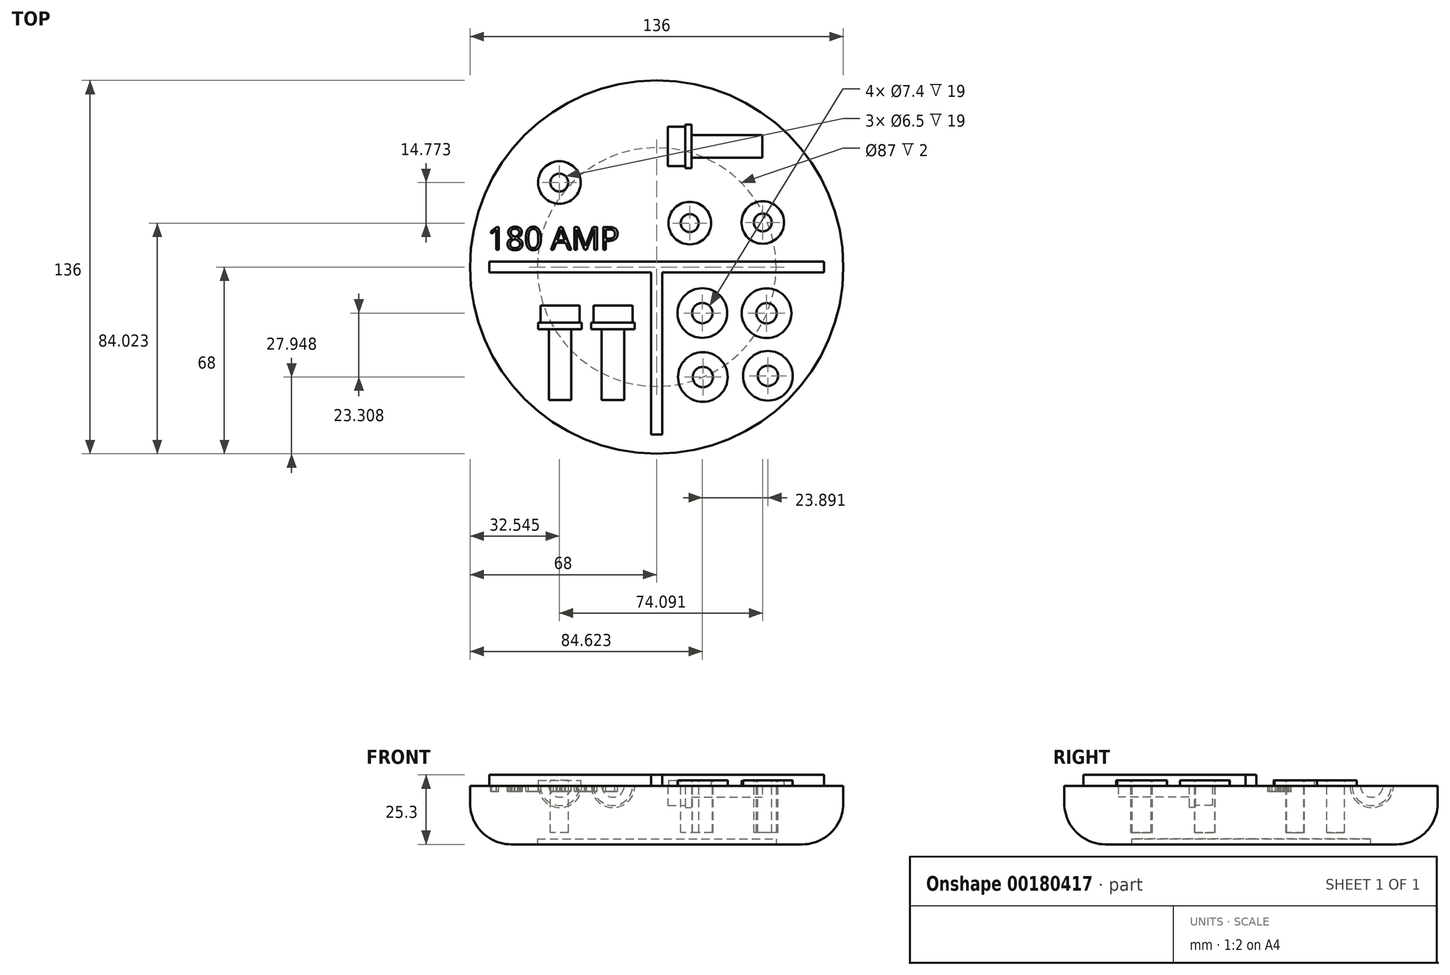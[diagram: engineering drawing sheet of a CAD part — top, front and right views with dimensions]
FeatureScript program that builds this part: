
annotation { "Feature Type Name" : "Feature", "Feature Type Description" : "" }
export const myFeature = defineFeature(function(context is Context, id is Id, definition is map)
    precondition{}
    {
        {
            var Q0;
            Q0=qCreatedBy(makeId("Front.planeOp"),FACE);
            var sketch = newSketch(context, id + "F0", { "sketchPlane" : qUnion([Q0])});
            skLineSegment(sketch, "E0.bottom", {"start": v(0, 0) * mm, "end": v(-68, 0) * mm});
            skLineSegment(sketch, "E0.top", {"start": v(0, -21.3) * mm, "end": v(-53, -21.3) * mm});
            skLineSegment(sketch, "E0.left", {"start": v(0, 0) * mm, "end": v(0, -21.3) * mm});
            skLineSegment(sketch, "E0.right", {"start": v(-68, 0) * mm, "end": v(-68, -6.3) * mm});
            skLineSegment(sketch, "E1.bottom", {"start": v(0, -21.3) * mm, "end": v(-43, -21.3) * mm});
            skLineSegment(sketch, "E1.top", {"start": v(0, -19.3) * mm, "end": v(-43, -19.3) * mm});
            skLineSegment(sketch, "E1.left", {"start": v(0, -21.3) * mm, "end": v(0, -19.3) * mm});
            skLineSegment(sketch, "E1.right", {"start": v(-43, -21.3) * mm, "end": v(-43, -19.3) * mm});
            skPoint(sketch, "E2.visualSharp", {"position": v(-68, -21.3) * mm});
            skArc(sketch, "E2.filletArc", {"start": v(-68, -6.3) * mm, "mid": v(-63.6, -16.9) * mm, "end": v(-53, -21.3) * mm});
            skSolve(sketch);
        }
        {
            var Q0;
            Q0=qSketchRegion(id+"F0",true);
            var Q1;
            Q1=sQuery(id+"F0.wireOp",EDGE,"E1.left");
            revolve(context, id + "F1", {"entities" : qUnion([Q0]), "axis" : qUnion([Q1]), "revolveType" : RevolveType.FULL});
        }
        {
            var Q0;
            Q0=makeQuery(id+"F1.opRevolve","SWEPT_FACE",FACE,{"disambiguationData":[OSD([sQuery(id+"F0.wireOp",EDGE,"E0.top"),sQuery(id+"F0.wireOp",EDGE,"E1.bottom")])]});
            var sketch = newSketch(context, id + "F2", { "sketchPlane" : qUnion([Q0])});
            skCircle(sketch, "E3", {"center": v(0, 0) * mm, "radius": 43.5 * mm});
            skSolve(sketch);
        }
        {
            var Q0;
            Q0=makeQuery(id+"F2.imprint","IMPRINT",FACE,{"disambiguationData":[TD([[makeQuery(id+"F2.imprint","IMPRINT",EDGE,{"derivedFrom":sQuery(id+"F2.wireOp",EDGE,"E3")}),1.0]])]});
            extrude(context, id + "F3", {"entities" : qUnion([Q0]), "operationType" : NewBodyOperationType.REMOVE, "oppositeDirection" : true, "depth" : 2 * mm});
        }
        {
            var Q0;
            Q0=makeQuery(id+"F1.opRevolve","SWEPT_FACE",FACE,{"disambiguationData":[OSD([sQuery(id+"F0.wireOp",EDGE,"E0.bottom")])]});
            var sketch = newSketch(context, id + "F4", { "sketchPlane" : qUnion([Q0])});
            skLineSegment(sketch, "E4", {"start": v(0, 0) * mm, "end": v(0, -68) * mm, "construction": true});
            skLineSegment(sketch, "E5.bottom", {"start": v(-2, 1.01) * mm, "end": v(2, 1.01) * mm});
            skLineSegment(sketch, "E5.top", {"start": v(-2, -60.99) * mm, "end": v(2, -60.99) * mm});
            skLineSegment(sketch, "E5.left", {"start": v(-2, 1.01) * mm, "end": v(-2, -60.99) * mm});
            skLineSegment(sketch, "E5.right", {"start": v(2, 1.01) * mm, "end": v(2, -60.99) * mm});
            skLineSegment(sketch, "E6.bottom", {"start": v(-61.02, 2) * mm, "end": v(60.99, 2) * mm});
            skLineSegment(sketch, "E6.top", {"start": v(-61.02, -2) * mm, "end": v(60.99, -2) * mm});
            skLineSegment(sketch, "E6.left", {"start": v(-61.02, 2) * mm, "end": v(-61.02, -2) * mm});
            skLineSegment(sketch, "E6.right", {"start": v(60.99, 2) * mm, "end": v(60.99, -2) * mm});
            skSolve(sketch);
        }
        {
            var Q0;
            {var subQ1=sQuery(id+"F4.wireOp",EDGE,"E5.bottom");Q0=makeQuery(id+"F4.imprint","IMPRINT",FACE,{"disambiguationData":[TD([[makeQuery(id+"F4.imprint","IMPRINT",EDGE,{"derivedFrom":subQ1}),1.0]])]});}
            var Q1;
            Q1=qSketchRegion(id+"F4",true);
            extrude(context, id + "F5", {"entities" : qUnion([Q0, Q1]), "operationType" : NewBodyOperationType.ADD, "depth" : 4 * mm});
        }
        {
            var Q0;
            Q0=makeQuery(id+"F1.opRevolve","SWEPT_FACE",FACE,{"disambiguationData":[OSD([sQuery(id+"F0.wireOp",EDGE,"E0.bottom")])]});
            var sketch = newSketch(context, id + "F6", { "sketchPlane" : qUnion([Q0])});
            skText(sketch, "E7", { "text": "180 AMP", "fontName": "OpenSans-Regular.ttf"});
            const initialGuessF6  = {"E7": [-0.0616, 0.00625, 1, 0, 0.0084]};
            skSetInitialGuess(sketch, initialGuessF6);
            skSolve(sketch);
        }
        {
            var Q0;
            Q0=qSketchRegion(id+"F6",true);
            extrude(context, id + "F7", {"entities" : qUnion([Q0]), "operationType" : NewBodyOperationType.REMOVE, "oppositeDirection" : true, "depth" : 2 * mm});
        }
        {
            var Q0;
            Q0=makeQuery(id+"F7.boolean.opBoolean","SPLIT",FACE,{"disambiguationData":[TD([makeQuery(id+"F1.opRevolve","SWEPT_FACE",FACE,{"disambiguationData":[OSD([sQuery(id+"F0.wireOp",EDGE,"E0.right")])]})])],"derivedFrom":makeQuery(id+"F1.opRevolve","SWEPT_FACE",FACE,{"disambiguationData":[OSD([sQuery(id+"F0.wireOp",EDGE,"E0.bottom")])]})});
            var sketch = newSketch(context, id + "F8", { "sketchPlane" : qUnion([Q0])});
            skCircle(sketch, "E8", {"center": v(-35.45, 30.8) * mm, "radius": 7.75 * mm});
            skSolve(sketch);
        }
        {
            var Q0;
            Q0=makeQuery(id+"F8.imprint","IMPRINT",FACE,{"disambiguationData":[TD([[makeQuery(id+"F8.imprint","IMPRINT",EDGE,{"derivedFrom":sQuery(id+"F8.wireOp",EDGE,"E8")}),1.0]])]});
            var sketch = newSketch(context, id + "F9", { "sketchPlane" : qUnion([Q0])});
            skSolve(sketch);
        }
        {
            var Q0;
            Q0=makeQuery(id+"F9.imprint","IMPRINT",FACE,{"disambiguationData":[TD([[makeQuery(id+"F9.imprint","IMPRINT",EDGE,{"derivedFrom":makeQuery(id+"F8.imprint","IMPRINT",EDGE,{"derivedFrom":sQuery(id+"F8.wireOp",EDGE,"E8")})}),1.0]])]});
            var Q1;
            Q1=qConstructionFilter(qBodyType(qCreatedBy(id+"F9",EDGE),BodyType.WIRE),ConstructionObject.NO);
            extrude(context, id + "F10", {"entities" : qUnion([Q0]), "operationType" : NewBodyOperationType.ADD, "surfaceEntities" : qUnion([Q1]), "depth" : 2 * mm});
        }
        {
            var Q0;
            Q0=makeQuery(id+"F8.imprint","IMPRINT",FACE,{"disambiguationData":[TD([[makeQuery(id+"F8.imprint","IMPRINT",EDGE,{"derivedFrom":sQuery(id+"F8.wireOp",EDGE,"E8")}),1.0]])]});
            extrude(context, id + "F11", {"entities" : qUnion([Q0]), "operationType" : NewBodyOperationType.ADD, "depth" : 2 * mm});
        }
        {
            var Q0;
            Q0=makeQuery(id+"F10.opExtrude","CAP_FACE",FACE,{"disambiguationData":[OSD([sQuery(id+"F8.wireOp",EDGE,"E8")])],"isStart":false});
            var sketch = newSketch(context, id + "F12", { "sketchPlane" : qUnion([Q0])});
            skCircle(sketch, "E9", {"center": v(-35.45, 30.8) * mm, "radius": 3.25 * mm});
            skSolve(sketch);
        }
        {
            var Q0;
            Q0=makeQuery(id+"F12.imprint","IMPRINT",FACE,{"disambiguationData":[TD([[makeQuery(id+"F12.imprint","IMPRINT",EDGE,{"derivedFrom":sQuery(id+"F12.wireOp",EDGE,"E9")}),1.0]])]});
            extrude(context, id + "F13", {"entities" : qUnion([Q0]), "operationType" : NewBodyOperationType.REMOVE, "oppositeDirection" : true, "depth" : 19 * mm});
        }
        {
            var Q0;
            Q0=makeQuery(id+"F7.boolean.opBoolean","SPLIT",FACE,{"disambiguationData":[TD([makeQuery(id+"F1.opRevolve","SWEPT_FACE",FACE,{"disambiguationData":[OSD([sQuery(id+"F0.wireOp",EDGE,"E0.right")])]})])],"derivedFrom":makeQuery(id+"F1.opRevolve","SWEPT_FACE",FACE,{"disambiguationData":[OSD([sQuery(id+"F0.wireOp",EDGE,"E0.bottom")])]})});
            var sketch = newSketch(context, id + "F14", { "sketchPlane" : qUnion([Q0])});
            skCircle(sketch, "E10", {"center": v(12.05, 16.02) * mm, "radius": 7.75 * mm});
            skSolve(sketch);
        }
        {
            var Q0;
            Q0=qSketchRegion(id+"F14",true);
            extrude(context, id + "F15", {"entities" : qUnion([Q0]), "operationType" : NewBodyOperationType.ADD, "depth" : 2 * mm});
        }
        {
            var Q0;
            Q0=makeQuery(id+"F15.opExtrude","CAP_FACE",FACE,{"disambiguationData":[OSD([sQuery(id+"F14.wireOp",EDGE,"E10")])],"isStart":false});
            var sketch = newSketch(context, id + "F16", { "sketchPlane" : qUnion([Q0])});
            skCircle(sketch, "E11", {"center": v(12.05, 16.02) * mm, "radius": 3.25 * mm});
            skSolve(sketch);
        }
        {
            var Q0;
            Q0=qSketchRegion(id+"F16",true);
            extrude(context, id + "F17", {"entities" : qUnion([Q0]), "operationType" : NewBodyOperationType.REMOVE, "oppositeDirection" : true, "depth" : 19 * mm});
        }
        {
            var Q0;
            Q0=makeQuery(id+"F7.boolean.opBoolean","SPLIT",FACE,{"disambiguationData":[TD([makeQuery(id+"F1.opRevolve","SWEPT_FACE",FACE,{"disambiguationData":[OSD([sQuery(id+"F0.wireOp",EDGE,"E0.right")])]})])],"derivedFrom":makeQuery(id+"F1.opRevolve","SWEPT_FACE",FACE,{"disambiguationData":[OSD([sQuery(id+"F0.wireOp",EDGE,"E0.bottom")])]})});
            var sketch = newSketch(context, id + "F18", { "sketchPlane" : qUnion([Q0])});
            skCircle(sketch, "E12", {"center": v(38.64, 16.25) * mm, "radius": 7.75 * mm});
            skSolve(sketch);
        }
        {
            var Q0;
            Q0=qSketchRegion(id+"F18",true);
            extrude(context, id + "F19", {"entities" : qUnion([Q0]), "operationType" : NewBodyOperationType.ADD, "depth" : 2 * mm});
        }
        {
            var Q0;
            Q0=makeQuery(id+"F19.opExtrude","CAP_FACE",FACE,{"disambiguationData":[OSD([sQuery(id+"F18.wireOp",EDGE,"E12")])],"isStart":false});
            var sketch = newSketch(context, id + "F20", { "sketchPlane" : qUnion([Q0])});
            skCircle(sketch, "E13", {"center": v(38.64, 16.25) * mm, "radius": 3.25 * mm});
            skSolve(sketch);
        }
        {
            var Q0;
            Q0=qSketchRegion(id+"F20",true);
            extrude(context, id + "F21", {"entities" : qUnion([Q0]), "operationType" : NewBodyOperationType.REMOVE, "oppositeDirection" : true, "depth" : 19 * mm});
        }
        {
            var Q0;
            Q0=makeQuery(id+"F7.boolean.opBoolean","SPLIT",FACE,{"disambiguationData":[TD([makeQuery(id+"F1.opRevolve","SWEPT_FACE",FACE,{"disambiguationData":[OSD([sQuery(id+"F0.wireOp",EDGE,"E0.right")])]})])],"derivedFrom":makeQuery(id+"F1.opRevolve","SWEPT_FACE",FACE,{"disambiguationData":[OSD([sQuery(id+"F0.wireOp",EDGE,"E0.bottom")])]})});
            var sketch = newSketch(context, id + "F22", { "sketchPlane" : qUnion([Q0])});
            skLineSegment(sketch, "E14", {"start": v(4.1, 43.98) * mm, "end": v(38.44, 43.98) * mm, "construction": true});
            skLineSegment(sketch, "E15.bottom", {"start": v(4.1, 43.98) * mm, "end": v(10.34, 43.98) * mm});
            skLineSegment(sketch, "E15.top", {"start": v(4.1, 36.85) * mm, "end": v(10.34, 36.85) * mm});
            skLineSegment(sketch, "E15.left", {"start": v(4.1, 43.98) * mm, "end": v(4.1, 36.85) * mm});
            skLineSegment(sketch, "E15.right", {"start": v(10.34, 40.41) * mm, "end": v(10.34, 36.85) * mm});
            skPoint(sketch, "E16.oppositeSnap0", {"position": v(10.34, 40.41) * mm});
            skLineSegment(sketch, "E16.bottom", {"start": v(10.34, 43.98) * mm, "end": v(12.7, 43.98) * mm});
            skLineSegment(sketch, "E16.top", {"start": v(10.34, 36.05) * mm, "end": v(12.7, 36.05) * mm});
            skLineSegment(sketch, "E16.left", {"start": v(10.34, 36.85) * mm, "end": v(10.34, 36.05) * mm});
            skLineSegment(sketch, "E16.right", {"start": v(12.7, 39.88) * mm, "end": v(12.7, 36.05) * mm});
            skLineSegment(sketch, "E17.bottom", {"start": v(12.7, 43.98) * mm, "end": v(38.44, 43.98) * mm});
            skLineSegment(sketch, "E17.top", {"start": v(12.7, 39.88) * mm, "end": v(38.44, 39.88) * mm});
            skLineSegment(sketch, "E17.right", {"start": v(38.44, 43.98) * mm, "end": v(38.44, 39.88) * mm});
            skPoint(sketch, "E18.orphan", {"position": v(0, 43.98) * mm});
            skSolve(sketch);
        }
        {
            var Q0;
            Q0=makeQuery(id+"F22.imprint","IMPRINT",FACE,{"disambiguationData":[TD([[makeQuery(id+"F22.imprint","IMPRINT",EDGE,{"derivedFrom":sQuery(id+"F22.wireOp",EDGE,"E15.bottom")}),-1.0]])]});
            var Q1;
            Q1=sQuery(id+"F22.wireOp",EDGE,"E17.bottom");
            revolve(context, id + "F23", {"operationType" : NewBodyOperationType.REMOVE, "entities" : qUnion([Q0]), "axis" : qUnion([Q1]), "revolveType" : RevolveType.FULL, "oppositeDirection" : true});
        }
        {
            var Q0;
            Q0=makeQuery(id+"F7.boolean.opBoolean","SPLIT",FACE,{"disambiguationData":[TD([makeQuery(id+"F1.opRevolve","SWEPT_FACE",FACE,{"disambiguationData":[OSD([sQuery(id+"F0.wireOp",EDGE,"E0.right")])]})])],"derivedFrom":makeQuery(id+"F1.opRevolve","SWEPT_FACE",FACE,{"disambiguationData":[OSD([sQuery(id+"F0.wireOp",EDGE,"E0.bottom")])]})});
            var sketch = newSketch(context, id + "F24", { "sketchPlane" : qUnion([Q0])});
            skLineSegment(sketch, "E19", {"start": v(-8.8, -14.01) * mm, "end": v(-15.93, -14.01) * mm, "construction": true});
            skLineSegment(sketch, "E20.left", {"start": v(-8.8, -14.01) * mm, "end": v(-8.8, -20.26) * mm, "construction": true});
            skLineSegment(sketch, "E20.right", {"start": v(-15.93, -14.01) * mm, "end": v(-15.93, -20.26) * mm, "construction": true});
            skLineSegment(sketch, "E21.bottom", {"start": v(-8.8, -20.26) * mm, "end": v(-8, -20.26) * mm, "construction": true});
            skLineSegment(sketch, "E21.top", {"start": v(-11.83, -22.61) * mm, "end": v(-8, -22.61) * mm, "construction": true});
            skLineSegment(sketch, "E21.left", {"start": v(-15.93, -20.26) * mm, "end": v(-15.93, -22.61) * mm, "construction": true});
            skLineSegment(sketch, "E21.right", {"start": v(-8, -20.26) * mm, "end": v(-8, -22.61) * mm, "construction": true});
            skLineSegment(sketch, "E22.top", {"start": v(-15.93, -48.36) * mm, "end": v(-11.83, -48.36) * mm});
            skLineSegment(sketch, "E22.left", {"start": v(-15.93, -22.61) * mm, "end": v(-15.93, -48.36) * mm});
            skLineSegment(sketch, "E22.right", {"start": v(-11.83, -22.61) * mm, "end": v(-11.83, -48.36) * mm});
            skLineSegment(sketch, "E23.bottom", {"start": v(-15.93, -14.01) * mm, "end": v(-8.8, -14.01) * mm});
            skLineSegment(sketch, "E23.left", {"start": v(-15.93, -14.01) * mm, "end": v(-15.93, -20.26) * mm});
            skLineSegment(sketch, "E23.right", {"start": v(-8.8, -14.01) * mm, "end": v(-8.8, -20.26) * mm});
            skLineSegment(sketch, "E24.bottom", {"start": v(-8, -20.26) * mm, "end": v(-8.8, -20.26) * mm});
            skLineSegment(sketch, "E24.top", {"start": v(-8, -22.61) * mm, "end": v(-11.83, -22.61) * mm});
            skLineSegment(sketch, "E24.left", {"start": v(-8, -20.26) * mm, "end": v(-8, -22.61) * mm});
            skLineSegment(sketch, "E24.right", {"start": v(-15.93, -20.26) * mm, "end": v(-15.93, -22.61) * mm});
            skSolve(sketch);
        }
        {
            var Q0;
            Q0=qSketchRegion(id+"F24",true);
            var Q1;
            Q1=sQuery(id+"F24.wireOp",EDGE,"E22.left");
            revolve(context, id + "F25", {"operationType" : NewBodyOperationType.REMOVE, "entities" : qUnion([Q0]), "axis" : qUnion([Q1]), "revolveType" : RevolveType.FULL, "oppositeDirection" : true});
        }
        {
            var Q0;
            Q0=makeQuery(id+"F7.boolean.opBoolean","SPLIT",FACE,{"disambiguationData":[TD([makeQuery(id+"F1.opRevolve","SWEPT_FACE",FACE,{"disambiguationData":[OSD([sQuery(id+"F0.wireOp",EDGE,"E0.right")])]})])],"derivedFrom":makeQuery(id+"F1.opRevolve","SWEPT_FACE",FACE,{"disambiguationData":[OSD([sQuery(id+"F0.wireOp",EDGE,"E0.bottom")])]})});
            var sketch = newSketch(context, id + "F26", { "sketchPlane" : qUnion([Q0])});
            skLineSegment(sketch, "E25", {"start": v(-8.8, -14.01) * mm, "end": v(-54.14, -14.01) * mm, "construction": true});
            skLineSegment(sketch, "E26.bottom", {"start": v(-28.05, -14.01) * mm, "end": v(-35.2, -14.01) * mm, "construction": true});
            skLineSegment(sketch, "E26.left", {"start": v(-28.05, -14.01) * mm, "end": v(-28.05, -20.26) * mm, "construction": true});
            skLineSegment(sketch, "E26.right", {"start": v(-35.2, -14.01) * mm, "end": v(-35.2, -20.26) * mm, "construction": true});
            skLineSegment(sketch, "E27.bottom", {"start": v(-35.2, -14.01) * mm, "end": v(-28.05, -14.01) * mm});
            skLineSegment(sketch, "E27.left", {"start": v(-35.2, -14.01) * mm, "end": v(-35.2, -20.26) * mm});
            skLineSegment(sketch, "E27.right", {"start": v(-28.05, -14.01) * mm, "end": v(-28.05, -20.26) * mm});
            skLineSegment(sketch, "E28.bottom", {"start": v(-28.05, -20.26) * mm, "end": v(-27.28, -20.26) * mm});
            skLineSegment(sketch, "E28.top", {"start": v(-31.1, -22.61) * mm, "end": v(-27.28, -22.61) * mm});
            skLineSegment(sketch, "E28.left", {"start": v(-35.2, -20.26) * mm, "end": v(-35.2, -22.61) * mm});
            skLineSegment(sketch, "E28.right", {"start": v(-27.28, -20.26) * mm, "end": v(-27.28, -22.61) * mm});
            skLineSegment(sketch, "E29.top", {"start": v(-35.2, -48.36) * mm, "end": v(-31.1, -48.36) * mm});
            skLineSegment(sketch, "E29.left", {"start": v(-35.2, -22.61) * mm, "end": v(-35.2, -48.36) * mm});
            skLineSegment(sketch, "E29.right", {"start": v(-31.1, -22.61) * mm, "end": v(-31.1, -48.36) * mm});
            skSolve(sketch);
        }
        {
            var Q0;
            Q0=qSketchRegion(id+"F26",true);
            var Q1;
            Q1=sQuery(id+"F26.wireOp",EDGE,"E29.left");
            revolve(context, id + "F27", {"operationType" : NewBodyOperationType.REMOVE, "entities" : qUnion([Q0]), "axis" : qUnion([Q1]), "revolveType" : RevolveType.FULL, "oppositeDirection" : true});
        }
        {
            var Q0;
            Q0=makeQuery(id+"F7.boolean.opBoolean","SPLIT",FACE,{"disambiguationData":[TD([makeQuery(id+"F1.opRevolve","SWEPT_FACE",FACE,{"disambiguationData":[OSD([sQuery(id+"F0.wireOp",EDGE,"E0.right")])]})])],"derivedFrom":makeQuery(id+"F1.opRevolve","SWEPT_FACE",FACE,{"disambiguationData":[OSD([sQuery(id+"F0.wireOp",EDGE,"E0.bottom")])]})});
            var sketch = newSketch(context, id + "F28", { "sketchPlane" : qUnion([Q0])});
            skCircle(sketch, "E30", {"center": v(16.62, -16.74) * mm, "radius": 9.05 * mm});
            skSolve(sketch);
        }
        {
            var Q0;
            Q0=makeQuery(id+"F28.imprint","IMPRINT",FACE,{"disambiguationData":[TD([[makeQuery(id+"F28.imprint","IMPRINT",EDGE,{"derivedFrom":sQuery(id+"F28.wireOp",EDGE,"E30")}),-1.0]])]});
            var sketch = newSketch(context, id + "F29", { "sketchPlane" : qUnion([Q0])});
            skCircle(sketch, "E31", {"center": v(40.02, -16.81) * mm, "radius": 9.05 * mm});
            skSolve(sketch);
        }
        {
            var Q0;
            Q0=makeQuery(id+"F28.imprint","IMPRINT",FACE,{"disambiguationData":[TD([[makeQuery(id+"F28.imprint","IMPRINT",EDGE,{"derivedFrom":sQuery(id+"F28.wireOp",EDGE,"E30")}),-1.0]])]});
            var sketch = newSketch(context, id + "F30", { "sketchPlane" : qUnion([Q0])});
            skCircle(sketch, "E32", {"center": v(16.82, -40.05) * mm, "radius": 9.05 * mm});
            skSolve(sketch);
        }
        {
            var Q0;
            Q0=makeQuery(id+"F28.imprint","IMPRINT",FACE,{"disambiguationData":[TD([[makeQuery(id+"F28.imprint","IMPRINT",EDGE,{"derivedFrom":sQuery(id+"F28.wireOp",EDGE,"E30")}),-1.0]])]});
            var sketch = newSketch(context, id + "F31", { "sketchPlane" : qUnion([Q0])});
            skCircle(sketch, "E33", {"center": v(40.51, -39.6) * mm, "radius": 9.05 * mm});
            skSolve(sketch);
        }
        {
            var Q0;
            Q0=makeQuery(id+"F28.imprint","IMPRINT",FACE,{"disambiguationData":[TD([[makeQuery(id+"F28.imprint","IMPRINT",EDGE,{"derivedFrom":sQuery(id+"F28.wireOp",EDGE,"E30")}),1.0]])]});
            extrude(context, id + "F32", {"entities" : qUnion([Q0]), "operationType" : NewBodyOperationType.ADD, "depth" : 2 * mm});
        }
        {
            var Q0;
            Q0=makeQuery(id+"F29.imprint","IMPRINT",FACE,{"disambiguationData":[TD([[makeQuery(id+"F29.imprint","IMPRINT",EDGE,{"derivedFrom":sQuery(id+"F29.wireOp",EDGE,"E31")}),1.0]])]});
            var Q1;
            Q1=makeQuery(id+"F30.imprint","IMPRINT",FACE,{"disambiguationData":[TD([[makeQuery(id+"F30.imprint","IMPRINT",EDGE,{"derivedFrom":sQuery(id+"F30.wireOp",EDGE,"E32")}),1.0]])]});
            extrude(context, id + "F33", {"entities" : qUnion([Q0, Q1]), "operationType" : NewBodyOperationType.ADD, "depth" : 2 * mm});
        }
        {
            var Q0;
            Q0=makeQuery(id+"F31.imprint","IMPRINT",FACE,{"disambiguationData":[TD([[makeQuery(id+"F31.imprint","IMPRINT",EDGE,{"derivedFrom":sQuery(id+"F31.wireOp",EDGE,"E33")}),1.0]])]});
            extrude(context, id + "F34", {"entities" : qUnion([Q0]), "operationType" : NewBodyOperationType.ADD, "depth" : 2 * mm});
        }
        {
            var Q0;
            Q0=makeQuery(id+"F32.opExtrude","CAP_FACE",FACE,{"disambiguationData":[OSD([sQuery(id+"F28.wireOp",EDGE,"E30")])],"isStart":false});
            var sketch = newSketch(context, id + "F35", { "sketchPlane" : qUnion([Q0])});
            skCircle(sketch, "E34", {"center": v(16.62, -16.74) * mm, "radius": 3.7 * mm});
            skSolve(sketch);
        }
        {
            var Q0;
            Q0=makeQuery(id+"F33.opExtrude","CAP_FACE",FACE,{"disambiguationData":[OSD([sQuery(id+"F30.wireOp",EDGE,"E32")])],"isStart":false});
            var sketch = newSketch(context, id + "F36", { "sketchPlane" : qUnion([Q0])});
            skCircle(sketch, "E35", {"center": v(16.82, -40.05) * mm, "radius": 3.7 * mm});
            skSolve(sketch);
        }
        {
            var Q0;
            Q0=makeQuery(id+"F34.opExtrude","CAP_FACE",FACE,{"disambiguationData":[OSD([sQuery(id+"F31.wireOp",EDGE,"E33")])],"isStart":false});
            var sketch = newSketch(context, id + "F37", { "sketchPlane" : qUnion([Q0])});
            skCircle(sketch, "E36", {"center": v(40.51, -39.6) * mm, "radius": 3.7 * mm});
            skSolve(sketch);
        }
        {
            var Q0;
            Q0=makeQuery(id+"F33.opExtrude","CAP_FACE",FACE,{"disambiguationData":[OSD([sQuery(id+"F29.wireOp",EDGE,"E31")])],"isStart":false});
            var sketch = newSketch(context, id + "F38", { "sketchPlane" : qUnion([Q0])});
            skCircle(sketch, "E37", {"center": v(40.02, -16.81) * mm, "radius": 3.7 * mm});
            skSolve(sketch);
        }
        {
            var Q0;
            Q0=makeQuery(id+"F35.imprint","IMPRINT",FACE,{"disambiguationData":[TD([[makeQuery(id+"F35.imprint","IMPRINT",EDGE,{"derivedFrom":sQuery(id+"F35.wireOp",EDGE,"E34")}),1.0]])]});
            var Q1;
            Q1=makeQuery(id+"F38.imprint","IMPRINT",FACE,{"disambiguationData":[TD([[makeQuery(id+"F38.imprint","IMPRINT",EDGE,{"derivedFrom":sQuery(id+"F38.wireOp",EDGE,"E37")}),1.0]])]});
            var Q2;
            Q2=makeQuery(id+"F37.imprint","IMPRINT",FACE,{"disambiguationData":[TD([[makeQuery(id+"F37.imprint","IMPRINT",EDGE,{"derivedFrom":sQuery(id+"F37.wireOp",EDGE,"E36")}),1.0]])]});
            var Q3;
            Q3=makeQuery(id+"F36.imprint","IMPRINT",FACE,{"disambiguationData":[TD([[makeQuery(id+"F36.imprint","IMPRINT",EDGE,{"derivedFrom":sQuery(id+"F36.wireOp",EDGE,"E35")}),1.0]])]});
            extrude(context, id + "F39", {"entities" : qUnion([Q0, Q1, Q2, Q3]), "operationType" : NewBodyOperationType.REMOVE, "oppositeDirection" : true, "depth" : 19 * mm});
        }
    });
